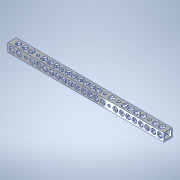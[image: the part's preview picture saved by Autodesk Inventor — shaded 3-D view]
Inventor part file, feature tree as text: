
AUTODESK INVENTOR PART (.ipt)
format: ipt  version: 2020.3 (Build 243373000, 373)  size: 318,464 bytes
history: native  units: mm
features: sketch x10, hole x7, extrude x3, other x1
ambient origin geometry x8: Origin, YZ Plane, XZ Plane, XY Plane, X Axis, Y Axis, Z Axis, Center Point
bodies: Body1 (feature_tree)
feature tree (21):
  other  "ソリッド1"
  extrude  "押し出し1"  Depth=9.0mm
  hole  "穴1"  [1 undecoded]
  hole  "穴2"  [1 undecoded]
  extrude  "押し出し2"  Depth=6.6mm
  extrude  "押し出し3"  Depth=1.2mm
  hole  "穴3"  [1 undecoded]
  hole  "穴4"  [1 undecoded]
  hole  "穴5"  [1 undecoded]
  hole  "穴6"  [1 undecoded]
  hole  "穴7"  [1 undecoded]
  sketch  "スケッチ1"
  sketch  "スケッチ2"
  sketch  "スケッチ3"
  sketch  "スケッチ4"
  sketch  "スケッチ5"
  sketch  "スケッチ6"
  sketch  "スケッチ7"
  sketch  "スケッチ8"
  sketch  "スケッチ9"
  sketch  "スケッチ10"
note: 7 required parameter values undecoded (feature->parameter linkage not recoverable at this tier; creation-order binding heuristic only, values carry confidence <= 0.55)
